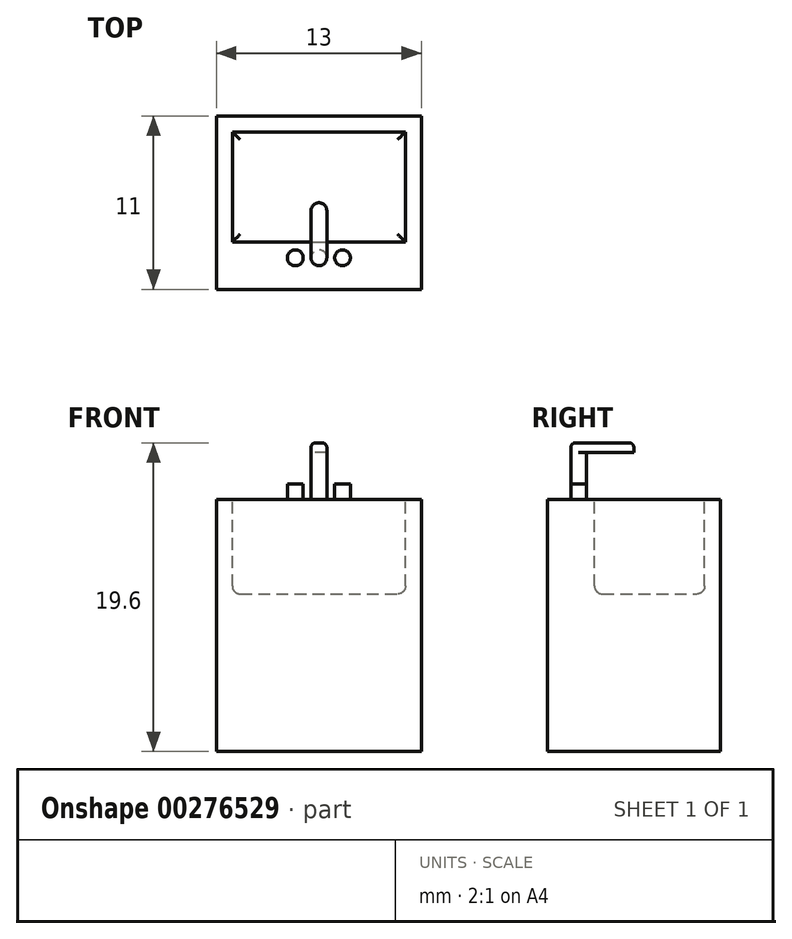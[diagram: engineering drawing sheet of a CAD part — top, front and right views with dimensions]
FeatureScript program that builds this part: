
annotation { "Feature Type Name" : "Feature", "Feature Type Description" : "" }
export const myFeature = defineFeature(function(context is Context, id is Id, definition is map)
    precondition{}
    {
        {
            var Q0;
            Q0=qCreatedBy(makeId("Top.planeOp"),FACE);
            var sketch = newSketch(context, id + "F0", { "sketchPlane" : qUnion([Q0])});
            skLineSegment(sketch, "E0.bottom", {"start": v(0, 11) * mm, "end": v(13, 11) * mm});
            skLineSegment(sketch, "E0.top", {"start": v(0, 0) * mm, "end": v(13, 0) * mm});
            skLineSegment(sketch, "E0.left", {"start": v(0, 11) * mm, "end": v(0, 0) * mm});
            skLineSegment(sketch, "E0.right", {"start": v(13, 11) * mm, "end": v(13, 0) * mm});
            skSolve(sketch);
        }
        {
            var Q0;
            Q0=makeQuery(id+"F0.imprint","IMPRINT",FACE,{"disambiguationData":[TD([[makeQuery(id+"F0.imprint","IMPRINT",EDGE,{"derivedFrom":sQuery(id+"F0.wireOp",EDGE,"E0.bottom")}),-1.0]])]});
            var Q1;
            Q1=makeQuery(id+"F0.imprint","IMPRINT",FACE,{"disambiguationData":[TD([[makeQuery(id+"F0.imprint","IMPRINT",EDGE,{"derivedFrom":sQuery(id+"F0.wireOp",EDGE,"bn0eEvJu-FUIQ-UbGs-vVTZ-7MZcTDpSjBkk.bottom")}),1.0]])]});
            extrude(context, id + "F1", {"entities" : qUnion([Q0, Q1]), "depth" : 16 * mm});
        }
        {
            var Q0;
            Q0=makeQuery(id+"F1.opExtrude","CAP_FACE",FACE,{"disambiguationData":[OSD([sQuery(id+"F0.wireOp",EDGE,"E0.bottom"),sQuery(id+"F0.wireOp",EDGE,"E0.top"),sQuery(id+"F0.wireOp",EDGE,"E0.left"),sQuery(id+"F0.wireOp",EDGE,"E0.right")])],"isStart":false});
            var sketch = newSketch(context, id + "F2", { "sketchPlane" : qUnion([Q0])});
            skLineSegment(sketch, "E1", {"start": v(1, 3) * mm, "end": v(12, 3) * mm});
            skPoint(sketch, "E2", {"position": v(6.5, 3) * mm});
            skLineSegment(sketch, "E3.top", {"start": v(1, 10) * mm, "end": v(12, 10) * mm});
            skLineSegment(sketch, "E3.left", {"start": v(1, 3) * mm, "end": v(1, 10) * mm});
            skLineSegment(sketch, "E4", {"start": v(12, 3) * mm, "end": v(12, 10) * mm});
            skSolve(sketch);
        }
        {
            var Q0;
            Q0=makeQuery(id+"F2.imprint","IMPRINT",FACE,{"disambiguationData":[TD([[makeQuery(id+"F2.imprint","IMPRINT",EDGE,{"derivedFrom":sQuery(id+"F2.wireOp",EDGE,"E1")}),1.0]])]});
            extrude(context, id + "F3", {"entities" : qUnion([Q0]), "operationType" : NewBodyOperationType.REMOVE, "oppositeDirection" : true, "depth" : 6 * mm});
        }
        {
            var Q0;
            Q0=makeQuery(id+"F3.boolean.opBoolean","COPY",FACE,{"derivedFrom":makeQuery(id+"F3.opExtrude","CAP_FACE",FACE,{"disambiguationData":[OSD([sQuery(id+"F2.wireOp",EDGE,"E1"),sQuery(id+"F2.wireOp",EDGE,"E3.top"),sQuery(id+"F2.wireOp",EDGE,"E3.left"),sQuery(id+"F2.wireOp",EDGE,"E4")])],"isStart":false})});
            fillet(context, id + "F4", {"entities" : qUnion([Q0]), "radius" : 0.5 * mm, "tangentPropagation" : true, "allowEdgeOverflow" : false});
        }
        {
            var Q0;
            Q0=makeQuery(id+"F1.opExtrude","CAP_FACE",FACE,{"disambiguationData":[OSD([sQuery(id+"F0.wireOp",EDGE,"E0.bottom"),sQuery(id+"F0.wireOp",EDGE,"E0.top"),sQuery(id+"F0.wireOp",EDGE,"E0.left"),sQuery(id+"F0.wireOp",EDGE,"E0.right")])],"isStart":false});
            var sketch = newSketch(context, id + "F5", { "sketchPlane" : qUnion([Q0])});
            skCircle(sketch, "E5", {"center": v(6.5, 2) * mm, "radius": 0.5 * mm});
            skPoint(sketch, "E5.centerSnap0", {"position": v(6.5, 3) * mm});
            skCircle(sketch, "E6", {"center": v(5, 2) * mm, "radius": 0.5 * mm});
            skCircle(sketch, "E7", {"center": v(8, 2) * mm, "radius": 0.5 * mm});
            skSolve(sketch);
        }
        {
            var Q0;
            Q0=makeQuery(id+"F5.imprint","IMPRINT",FACE,{"disambiguationData":[TD([[makeQuery(id+"F5.imprint","IMPRINT",EDGE,{"derivedFrom":sQuery(id+"F5.wireOp",EDGE,"E6")}),1.0]])]});
            var Q1;
            Q1=makeQuery(id+"F5.imprint","IMPRINT",FACE,{"disambiguationData":[TD([[makeQuery(id+"F5.imprint","IMPRINT",EDGE,{"derivedFrom":sQuery(id+"F5.wireOp",EDGE,"E7")}),1.0]])]});
            extrude(context, id + "F6", {"entities" : qUnion([Q0, Q1]), "operationType" : NewBodyOperationType.ADD, "depth" : 1 * mm});
        }
        {
            var Q0;
            Q0=makeQuery(id+"F5.imprint","IMPRINT",FACE,{"disambiguationData":[TD([[makeQuery(id+"F5.imprint","IMPRINT",EDGE,{"derivedFrom":sQuery(id+"F5.wireOp",EDGE,"E5")}),1.0]])]});
            extrude(context, id + "F7", {"entities" : qUnion([Q0]), "operationType" : NewBodyOperationType.ADD, "depth" : 3 * mm});
        }
        {
            var Q0;
            Q0=makeQuery(id+"F7.opExtrude","CAP_FACE",FACE,{"disambiguationData":[OSD([sQuery(id+"F5.wireOp",EDGE,"E5")])],"isStart":false});
            var sketch = newSketch(context, id + "F8", { "sketchPlane" : qUnion([Q0])});
            skArc(sketch, "E8", {"start": v(6, 2) * mm, "mid": v(6.5, 1.5) * mm, "end": v(7, 2) * mm});
            skLineSegment(sketch, "E9", {"start": v(6, 2) * mm, "end": v(6, 5) * mm});
            skLineSegment(sketch, "E10", {"start": v(7, 2) * mm, "end": v(7, 5) * mm});
            skArc(sketch, "E11", {"start": v(7, 5) * mm, "mid": v(6.5, 5.5) * mm, "end": v(6, 5) * mm});
            skSolve(sketch);
        }
        {
            var Q0;
            Q0 = qSketchRegion(id + "F8", true);
            extrude(context, id + "F9", {"entities" : qUnion([Q0]), "operationType" : NewBodyOperationType.ADD, "depth" : 0.6 * mm});
        }
        {
            var Q0;
            Q0=makeQuery(id+"F9.opExtrude","CAP_FACE",FACE,{"disambiguationData":[OSD([sQuery(id+"F8.wireOp",EDGE,"E8"),sQuery(id+"F8.wireOp",EDGE,"E9"),sQuery(id+"F8.wireOp",EDGE,"E10"),sQuery(id+"F8.wireOp",EDGE,"E11")])],"isStart":false});
            fillet(context, id + "F10", {"entities" : qUnion([Q0]), "radius" : 0.3 * mm, "tangentPropagation" : true, "allowEdgeOverflow" : false});
        }
    });
